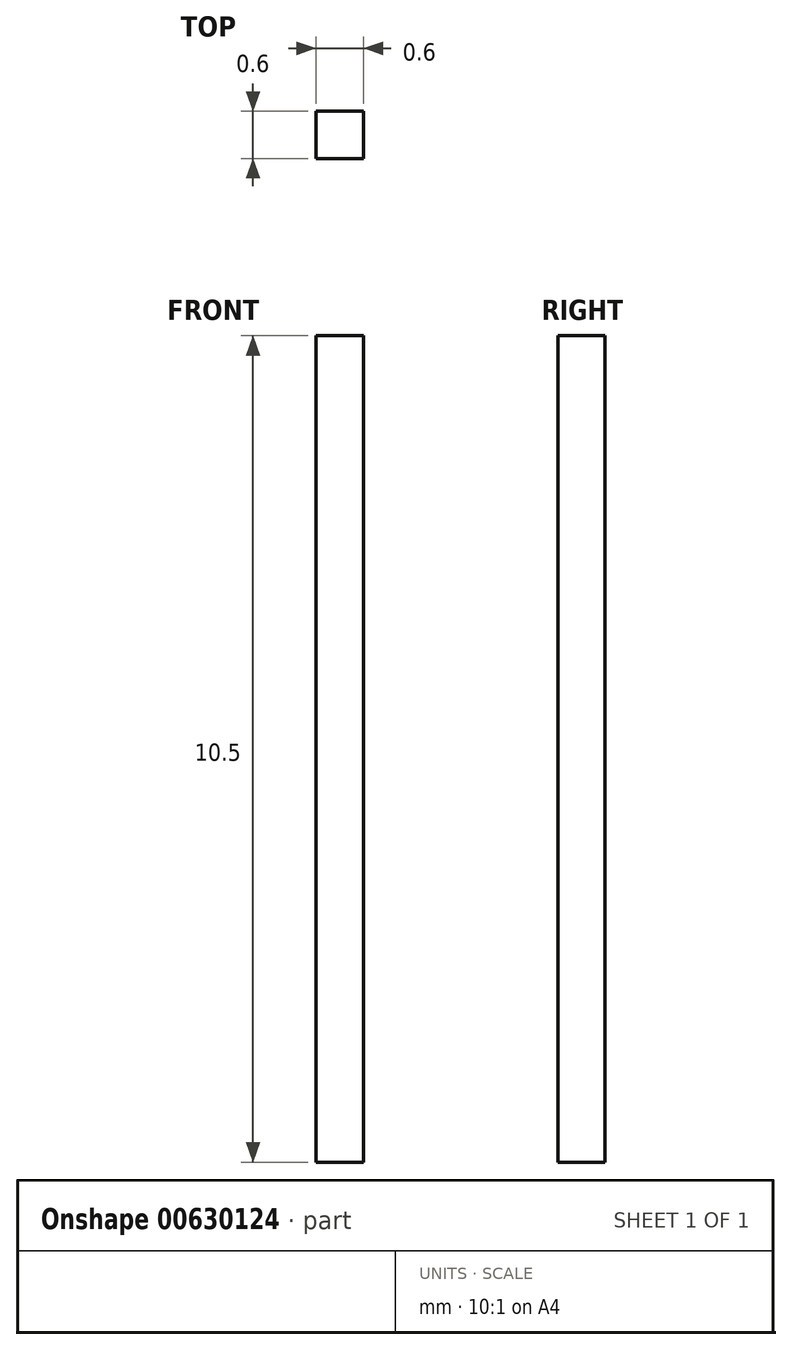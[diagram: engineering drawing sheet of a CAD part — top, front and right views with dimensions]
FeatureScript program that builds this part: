
annotation { "Feature Type Name" : "Feature", "Feature Type Description" : "" }
export const myFeature = defineFeature(function(context is Context, id is Id, definition is map)
    precondition{}
    {
        {
            var Q0;
            Q0=qCreatedBy(makeId("Top.planeOp"),FACE);
            var sketch = newSketch(context, id + "F0", { "sketchPlane" : qUnion([Q0])});
            skLineSegment(sketch, "E0.bottom", {"start": v(0, 0) * mm, "end": v(0.6, 0) * mm});
            skLineSegment(sketch, "E0.top", {"start": v(0, 0.6) * mm, "end": v(0.6, 0.6) * mm});
            skLineSegment(sketch, "E0.left", {"start": v(0, 0) * mm, "end": v(0, 0.6) * mm});
            skLineSegment(sketch, "E0.right", {"start": v(0.6, 0) * mm, "end": v(0.6, 0.6) * mm});
            skSolve(sketch);
        }
        {
            var Q0;
            Q0=qSketchRegion(id+"F0",true);
            extrude(context, id + "F1", {"entities" : qUnion([Q0]), "depth" : 10.5 * mm});
        }
    });
